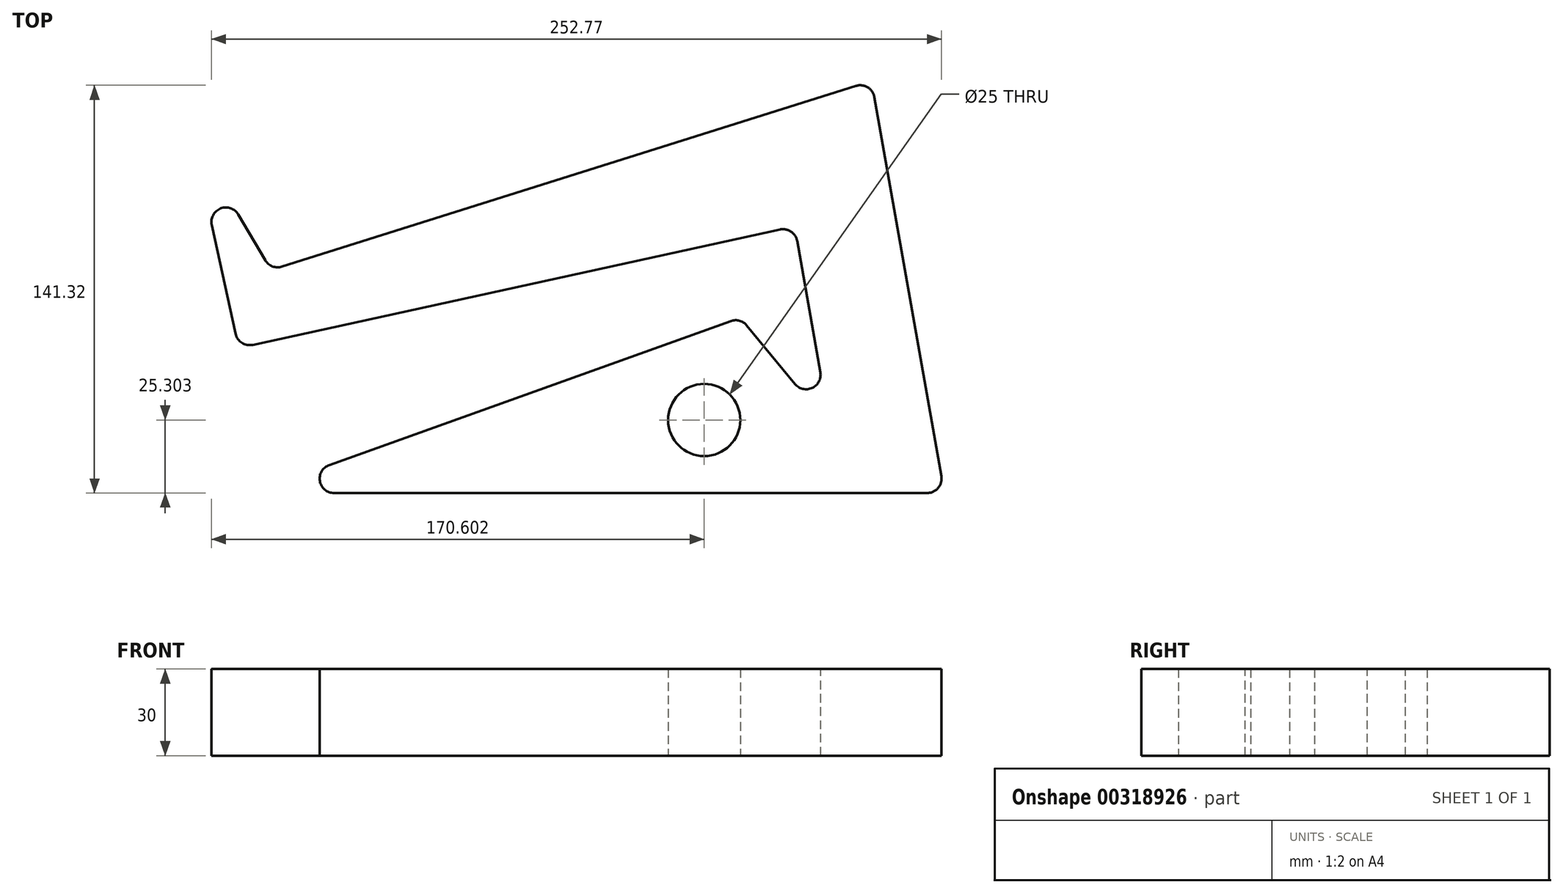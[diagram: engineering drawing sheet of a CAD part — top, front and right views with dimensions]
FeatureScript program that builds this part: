
annotation { "Feature Type Name" : "Feature", "Feature Type Description" : "" }
export const myFeature = defineFeature(function(context is Context, id is Id, definition is map)
    precondition{}
    {
        {
            var Q0;
            Q0=qCreatedBy(makeId("Top.planeOp"),FACE);
            var sketch = newSketch(context, id + "F0", { "sketchPlane" : qUnion([Q0])});
            skLineSegment(sketch, "E0", {"start": v(77.68, 72.5) * mm, "end": v(102.86, -70.3) * mm});
            skLineSegment(sketch, "E1", {"start": v(102.86, -70.3) * mm, "end": v(-137.14, -70.3) * mm});
            skLineSegment(sketch, "E2", {"start": v(-137.14, -70.3) * mm, "end": v(32.23, -9.5) * mm});
            skLineSegment(sketch, "E3", {"start": v(32.23, -9.5) * mm, "end": v(63.25, -47.22) * mm});
            skLineSegment(sketch, "E4", {"start": v(63.25, -47.22) * mm, "end": v(51.02, 22.14) * mm});
            skLineSegment(sketch, "E5", {"start": v(51.02, 22.14) * mm, "end": v(-141.42, -20.01) * mm});
            skLineSegment(sketch, "E6", {"start": v(-141.42, -20.01) * mm, "end": v(-157.47, 53.25) * mm});
            skLineSegment(sketch, "E7", {"start": v(-157.47, 53.25) * mm, "end": v(-130.23, 6.94) * mm});
            skLineSegment(sketch, "E8", {"start": v(-130.23, 6.94) * mm, "end": v(77.68, 72.5) * mm});
            skCircle(sketch, "E9", {"center": v(19.73, -45) * mm, "radius": 12.5 * mm});
            skSolve(sketch);
        }
        {
            var Q0;
            Q0=makeQuery(id+"F0.imprint","IMPRINT",FACE,{"disambiguationData":[TD([[makeQuery(id+"F0.imprint","IMPRINT",EDGE,{"derivedFrom":sQuery(id+"F0.wireOp",EDGE,"E0")}),-1.0]])]});
            extrude(context, id + "F1", {"entities" : qUnion([Q0]), "depth" : 30 * mm});
        }
        {
            var Q0;
            Q0=makeQuery(id+"F1.opExtrude","SWEPT_EDGE",EDGE,{"disambiguationData":[OSD([sQuery(id+"F0.wireOp",EDGE,"E7"),sQuery(id+"F0.wireOp",EDGE,"E8")])]});
            var Q1;
            Q1=makeQuery(id+"F1.opExtrude","SWEPT_EDGE",EDGE,{"disambiguationData":[OSD([sQuery(id+"F0.wireOp",EDGE,"E6"),sQuery(id+"F0.wireOp",EDGE,"E7")])]});
            var Q2;
            Q2=makeQuery(id+"F1.opExtrude","SWEPT_EDGE",EDGE,{"disambiguationData":[OSD([sQuery(id+"F0.wireOp",EDGE,"E5"),sQuery(id+"F0.wireOp",EDGE,"E6")])]});
            var Q3;
            Q3=makeQuery(id+"F1.opExtrude","SWEPT_EDGE",EDGE,{"disambiguationData":[OSD([sQuery(id+"F0.wireOp",EDGE,"E2"),sQuery(id+"F0.wireOp",EDGE,"E3")])]});
            var Q4;
            Q4=makeQuery(id+"F1.opExtrude","SWEPT_EDGE",EDGE,{"disambiguationData":[OSD([sQuery(id+"F0.wireOp",EDGE,"E3"),sQuery(id+"F0.wireOp",EDGE,"E4")])]});
            var Q5;
            Q5=makeQuery(id+"F1.opExtrude","SWEPT_EDGE",EDGE,{"disambiguationData":[OSD([sQuery(id+"F0.wireOp",EDGE,"E4"),sQuery(id+"F0.wireOp",EDGE,"E5")])]});
            var Q6;
            Q6=makeQuery(id+"F1.opExtrude","SWEPT_EDGE",EDGE,{"disambiguationData":[OSD([sQuery(id+"F0.wireOp",EDGE,"E1"),sQuery(id+"F0.wireOp",EDGE,"E2")])]});
            var Q7;
            Q7=makeQuery(id+"F1.opExtrude","SWEPT_EDGE",EDGE,{"disambiguationData":[OSD([sQuery(id+"F0.wireOp",EDGE,"E0"),sQuery(id+"F0.wireOp",EDGE,"E8")])]});
            var Q8;
            Q8=makeQuery(id+"F1.opExtrude","SWEPT_EDGE",EDGE,{"disambiguationData":[OSD([sQuery(id+"F0.wireOp",EDGE,"E0"),sQuery(id+"F0.wireOp",EDGE,"E1")])]});
            fillet(context, id + "F2", {"entities" : qUnion([Q0, Q1, Q2, Q3, Q4, Q5, Q6, Q7, Q8]), "radius" : 5 * mm, "tangentPropagation" : true, "allowEdgeOverflow" : false});
        }
    });
